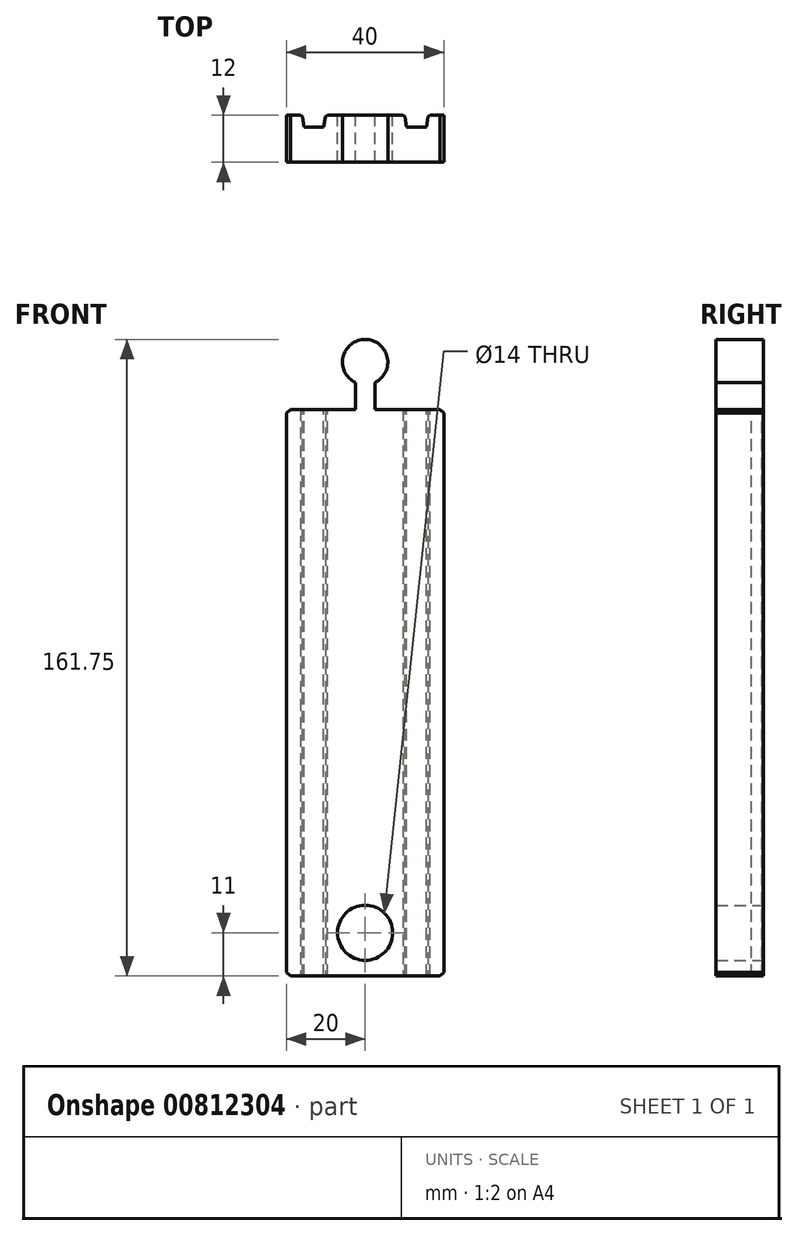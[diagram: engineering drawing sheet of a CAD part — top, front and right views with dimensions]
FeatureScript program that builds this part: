
annotation { "Feature Type Name" : "Feature", "Feature Type Description" : "" }
export const myFeature = defineFeature(function(context is Context, id is Id, definition is map)
    precondition{}
    {
        {
            var Q0;
            Q0=qCreatedBy(makeId("Top.planeOp"),FACE);
            var sketch = newSketch(context, id + "F0", { "sketchPlane" : qUnion([Q0])});
            skLineSegment(sketch, "E0.bottom", {"start": v(-20, 6) * mm, "end": v(20, 6) * mm});
            skLineSegment(sketch, "E0.top", {"start": v(-20, -6) * mm, "end": v(20, -6) * mm});
            skLineSegment(sketch, "E0.left", {"start": v(-20, 6) * mm, "end": v(-20, -6) * mm});
            skLineSegment(sketch, "E0.right", {"start": v(20, 6) * mm, "end": v(20, -6) * mm});
            skLineSegment(sketch, "E1", {"start": v(10.53, 3) * mm, "end": v(15.53, 3) * mm});
            skLineSegment(sketch, "E2", {"start": v(-15.53, 3) * mm, "end": v(-10.53, 3) * mm});
            skLineSegment(sketch, "E3", {"start": v(-20, 6) * mm, "end": v(20, -6) * mm, "construction": true});
            skLineSegment(sketch, "E4", {"start": v(-10.53, 3) * mm, "end": v(-10, 6) * mm});
            skLineSegment(sketch, "E5", {"start": v(-15.53, 3) * mm, "end": v(-16, 6) * mm});
            skLineSegment(sketch, "E6", {"start": v(10.53, 3) * mm, "end": v(10, 6) * mm});
            skLineSegment(sketch, "E7", {"start": v(15.53, 3) * mm, "end": v(16, 6) * mm});
            skSolve(sketch);
        }
        {
            var Q0;
            Q0=qCreatedBy(makeId("Front.planeOp"),FACE);
            var sketch = newSketch(context, id + "F1", { "sketchPlane" : qUnion([Q0])});
            skLineSegment(sketch, "E8", {"start": v(0, 144) * mm, "end": v(0, 0) * mm});
            skSolve(sketch);
        }
        {
            var Q0;
            Q0=makeQuery(id+"F0.imprint","IMPRINT",FACE,{"disambiguationData":[TD([[makeQuery(id+"F0.imprint","IMPRINT",EDGE,{"derivedFrom":sQuery(id+"F0.wireOp",EDGE,"E0.top")}),1.0]])]});
            var Q1;
            Q1=sQuery(id+"F1.wireOp",EDGE,"E8");
            sweep(context, id + "F2", {"profiles" : qUnion([Q0]), "path" : qUnion([Q1])});
        }
        {
            var Q0;
            Q0=makeQuery(id+"F2.opSweep","SWEPT_EDGE",EDGE,{"disambiguationData":[OSD([sQuery(id+"F0.wireOp",EDGE,"E0.bottom"),sQuery(id+"F0.wireOp",EDGE,"E4"),sQuery(id+"F1.wireOp",EDGE,"E8")])]});
            var Q1;
            Q1=makeQuery(id+"F2.opSweep","SWEPT_EDGE",EDGE,{"disambiguationData":[OSD([sQuery(id+"F0.wireOp",EDGE,"E0.bottom"),sQuery(id+"F0.wireOp",EDGE,"E5"),sQuery(id+"F1.wireOp",EDGE,"E8")])]});
            var Q2;
            Q2=makeQuery(id+"F2.opSweep","SWEPT_EDGE",EDGE,{"disambiguationData":[OSD([sQuery(id+"F0.wireOp",EDGE,"E0.bottom"),sQuery(id+"F0.wireOp",EDGE,"E6"),sQuery(id+"F1.wireOp",EDGE,"E8")])]});
            var Q3;
            Q3=makeQuery(id+"F2.opSweep","SWEPT_EDGE",EDGE,{"disambiguationData":[OSD([sQuery(id+"F0.wireOp",EDGE,"E0.bottom"),sQuery(id+"F0.wireOp",EDGE,"E7"),sQuery(id+"F1.wireOp",EDGE,"E8")])]});
            chamfer(context, id + "F3", {"entities" : qUnion([Q0, Q1, Q2, Q3]), "width" : 0.5 * mm, "tangentPropagation" : true});
        }
        {
            var Q0;
            Q0=qCreatedBy(makeId("Front.planeOp"),FACE);
            var sketch = newSketch(context, id + "F4", { "sketchPlane" : qUnion([Q0])});
            skLineSegment(sketch, "E9.0", {"start": v(9.5, 144) * mm, "end": v(-9.5, 144) * mm});
            skLineSegment(sketch, "E10", {"start": v(2.5, 144) * mm, "end": v(2.5, 151) * mm});
            skLineSegment(sketch, "E11", {"start": v(2.5, 151) * mm, "end": v(-2.5, 151) * mm});
            skLineSegment(sketch, "E12", {"start": v(-2.5, 151) * mm, "end": v(-2.5, 144) * mm});
            skLineSegment(sketch, "E13", {"start": v(2.5, 144) * mm, "end": v(9.5, 144) * mm, "construction": true});
            skLineSegment(sketch, "E14", {"start": v(-2.5, 144) * mm, "end": v(-9.5, 144) * mm, "construction": true});
            skPoint(sketch, "E15", {"position": v(0, 156) * mm});
            skCircle(sketch, "E16", {"center": v(0, 156) * mm, "radius": 5.75 * mm});
            skLineSegment(sketch, "E17", {"start": v(0, 144) * mm, "end": v(0, 168) * mm});
            skSolve(sketch);
        }
        {
            var Q0;
            Q0=qCreatedBy(makeId("Front.planeOp"),FACE);
            var sketch = newSketch(context, id + "F5", { "sketchPlane" : qUnion([Q0])});
            skLineSegment(sketch, "E18.0", {"start": v(9.5, 0) * mm, "end": v(-9.5, 0) * mm});
            skLineSegment(sketch, "E19.bottom", {"start": v(3.5, 0) * mm, "end": v(-3.5, 0) * mm});
            skLineSegment(sketch, "E19.top", {"start": v(3.5, 5) * mm, "end": v(-3.5, 5) * mm});
            skLineSegment(sketch, "E19.left", {"start": v(3.5, 0) * mm, "end": v(3.5, 5) * mm});
            skLineSegment(sketch, "E19.right", {"start": v(-3.5, 0) * mm, "end": v(-3.5, 5) * mm});
            skLineSegment(sketch, "E20", {"start": v(9.5, 0) * mm, "end": v(3.5, 0) * mm, "construction": true});
            skLineSegment(sketch, "E21", {"start": v(-3.5, 0) * mm, "end": v(-9.5, 0) * mm, "construction": true});
            skCircle(sketch, "E22", {"center": v(0, 11) * mm, "radius": 7 * mm});
            skPoint(sketch, "E22.centerSnap0", {"position": v(0, 5) * mm});
            skSolve(sketch);
        }
        {
            var Q0;
            {var subQ0=sQuery(id+"F1.wireOp",EDGE,"E8");var subQ1=sQuery(id+"F0.wireOp",EDGE,"E0.bottom");Q0=makeQuery(id+"F2.opSweep","SWEPT_FACE",FACE,{"disambiguationData":[OSD([subQ1,subQ0]),TDD([makeQuery(id+"F0.imprint","IMPRINT",EDGE,{"disambiguationData":[TD([[makeQuery(id+"F0.imprint","INTERSECT",VERTEX,{"derivedFrom":[subQ1,sQuery(id+"F0.wireOp",EDGE,"E4")]}),-1.0]])],"derivedFrom":subQ1}),subQ0])]});}
            var sketch = newSketch(context, id + "F6", { "sketchPlane" : qUnion([Q0])});
            skCircle(sketch, "E23.0", {"center": v(0, 11) * mm, "radius": 7 * mm});
            skLineSegment(sketch, "E24.0", {"start": v(3.5, 0) * mm, "end": v(3.5, 5) * mm});
            skLineSegment(sketch, "E25.0", {"start": v(-3.5, 0) * mm, "end": v(-3.5, 5) * mm});
            skLineSegment(sketch, "E26.0", {"start": v(-3.5, 5) * mm, "end": v(3.5, 5) * mm});
            skLineSegment(sketch, "E27.0", {"start": v(-9.5, 0) * mm, "end": v(9.5, 0) * mm});
            skSolve(sketch);
        }
        {
            var Q0;
            {var subQ5=sQuery(id+"F6.wireOp",EDGE,"E26.0");Q0=makeQuery(id+"F6.imprint","IMPRINT",FACE,{"disambiguationData":[TD([[makeQuery(id+"F6.imprint","IMPRINT",EDGE,{"derivedFrom":subQ5}),1.0]])]});}
            var Q1;
            {var subQ0=sQuery(id+"F6.wireOp",EDGE,"E24.0");var subQ1=sQuery(id+"F6.wireOp",EDGE,"E23.0");var subQ2=makeQuery(id+"F6.imprint","INTERSECT",VERTEX,{"derivedFrom":[subQ1,subQ0]});Q1=makeQuery(id+"F6.imprint","IMPRINT",FACE,{"disambiguationData":[TD([[makeQuery(id+"F6.imprint","IMPRINT",EDGE,{"disambiguationData":[TD([[subQ2,-1.0]])],"derivedFrom":subQ1}),1.0]])]});}
            var Q2;
            {var subQ5=sQuery(id+"F6.wireOp",EDGE,"E26.0");Q2=makeQuery(id+"F6.imprint","IMPRINT",FACE,{"disambiguationData":[TD([[makeQuery(id+"F6.imprint","IMPRINT",EDGE,{"derivedFrom":subQ5}),-1.0]])]});}
            extrude(context, id + "F7", {"entities" : qUnion([Q0, Q1, Q2]), "operationType" : NewBodyOperationType.REMOVE, "oppositeDirection" : true, "depth" : 25.4 * mm, "offsetDistance" : 25.4 * mm});
        }
        {
            var Q0;
            Q0=makeQuery(id+"F2.opSweep","CAP_EDGE",EDGE,{"disambiguationData":[OSD([sQuery(id+"F0.wireOp",EDGE,"E0.right"),sQuery(id+"F1.wireOp",VERTEX,"E8.start")])],"isStart":false});
            var Q1;
            Q1=makeQuery(id+"F2.opSweep","CAP_EDGE",EDGE,{"disambiguationData":[OSD([sQuery(id+"F0.wireOp",EDGE,"E0.left"),sQuery(id+"F1.wireOp",VERTEX,"E8.start")])],"isStart":false});
            var Q2;
            Q2=makeQuery(id+"F2.opSweep","CAP_EDGE",EDGE,{"disambiguationData":[OSD([sQuery(id+"F0.wireOp",EDGE,"E0.left"),sQuery(id+"F1.wireOp",VERTEX,"E8.end")])],"isStart":true});
            var Q3;
            Q3=makeQuery(id+"F2.opSweep","CAP_EDGE",EDGE,{"disambiguationData":[OSD([sQuery(id+"F0.wireOp",EDGE,"E0.right"),sQuery(id+"F1.wireOp",VERTEX,"E8.end")])],"isStart":true});
            chamfer(context, id + "F8", {"entities" : qUnion([Q0, Q1, Q2, Q3]), "width" : 1 * mm, "tangentPropagation" : true});
        }
        {
            var Q0;
            {var subQ0=sQuery(id+"F4.wireOp",EDGE,"E12");var subQ1=sQuery(id+"F4.wireOp",EDGE,"E11");var subQ2=makeQuery(id+"F4.imprint","INTERSECT",VERTEX,{"derivedFrom":[subQ1,subQ0]});Q0=makeQuery(id+"F4.imprint","IMPRINT",FACE,{"disambiguationData":[TD([[makeQuery(id+"F4.imprint","IMPRINT",EDGE,{"disambiguationData":[TD([[subQ2,1.0]])],"derivedFrom":subQ1}),-1.0]])]});}
            var Q1;
            {var subQ0=sQuery(id+"F4.wireOp",EDGE,"E10");var subQ1=sQuery(id+"F4.wireOp",EDGE,"E9.0");var subQ2=makeQuery(id+"F4.imprint","INTERSECT",VERTEX,{"derivedFrom":[subQ1,subQ0]});Q1=makeQuery(id+"F4.imprint","IMPRINT",FACE,{"disambiguationData":[TD([[makeQuery(id+"F4.imprint","IMPRINT",EDGE,{"disambiguationData":[TD([[subQ2,-1.0]])],"derivedFrom":subQ1}),-1.0]])]});}
            var Q2;
            {var subQ0=sQuery(id+"F4.wireOp",EDGE,"E12");var subQ1=sQuery(id+"F4.wireOp",EDGE,"E9.0");var subQ2=makeQuery(id+"F4.imprint","INTERSECT",VERTEX,{"derivedFrom":[subQ1,subQ0]});Q2=makeQuery(id+"F4.imprint","IMPRINT",FACE,{"disambiguationData":[TD([[makeQuery(id+"F4.imprint","IMPRINT",EDGE,{"disambiguationData":[TD([[subQ2,1.0]])],"derivedFrom":subQ1}),-1.0]])]});}
            var Q3;
            {var subQ0=sQuery(id+"F4.wireOp",EDGE,"E12");var subQ1=sQuery(id+"F4.wireOp",EDGE,"E11");var subQ2=makeQuery(id+"F4.imprint","INTERSECT",VERTEX,{"derivedFrom":[subQ1,subQ0]});Q3=makeQuery(id+"F4.imprint","IMPRINT",FACE,{"disambiguationData":[TD([[makeQuery(id+"F4.imprint","IMPRINT",EDGE,{"disambiguationData":[TD([[subQ2,1.0]])],"derivedFrom":subQ1}),1.0]])]});}
            var Q4;
            {var subQ0=sQuery(id+"F4.wireOp",EDGE,"E11");var subQ1=sQuery(id+"F4.wireOp",EDGE,"E10");var subQ2=makeQuery(id+"F4.imprint","INTERSECT",VERTEX,{"derivedFrom":[subQ1,subQ0]});Q4=makeQuery(id+"F4.imprint","IMPRINT",FACE,{"disambiguationData":[TD([[makeQuery(id+"F4.imprint","IMPRINT",EDGE,{"disambiguationData":[TD([[subQ2,1.0]])],"derivedFrom":subQ1}),-1.0]])]});}
            var Q5;
            {var subQ0=sQuery(id+"F4.wireOp",EDGE,"E11");var subQ1=sQuery(id+"F4.wireOp",EDGE,"E10");var subQ2=makeQuery(id+"F4.imprint","INTERSECT",VERTEX,{"derivedFrom":[subQ1,subQ0]});Q5=makeQuery(id+"F4.imprint","IMPRINT",FACE,{"disambiguationData":[TD([[makeQuery(id+"F4.imprint","IMPRINT",EDGE,{"disambiguationData":[TD([[subQ2,1.0]])],"derivedFrom":subQ1}),1.0]])]});}
            extrude(context, id + "F9", {"entities" : qUnion([Q0, Q1, Q2, Q3, Q4, Q5]), "operationType" : NewBodyOperationType.ADD, "endBound" : BoundingType.SYMMETRIC, "depth" : 12 * mm, "offsetDistance" : 25.4 * mm});
        }
    });
